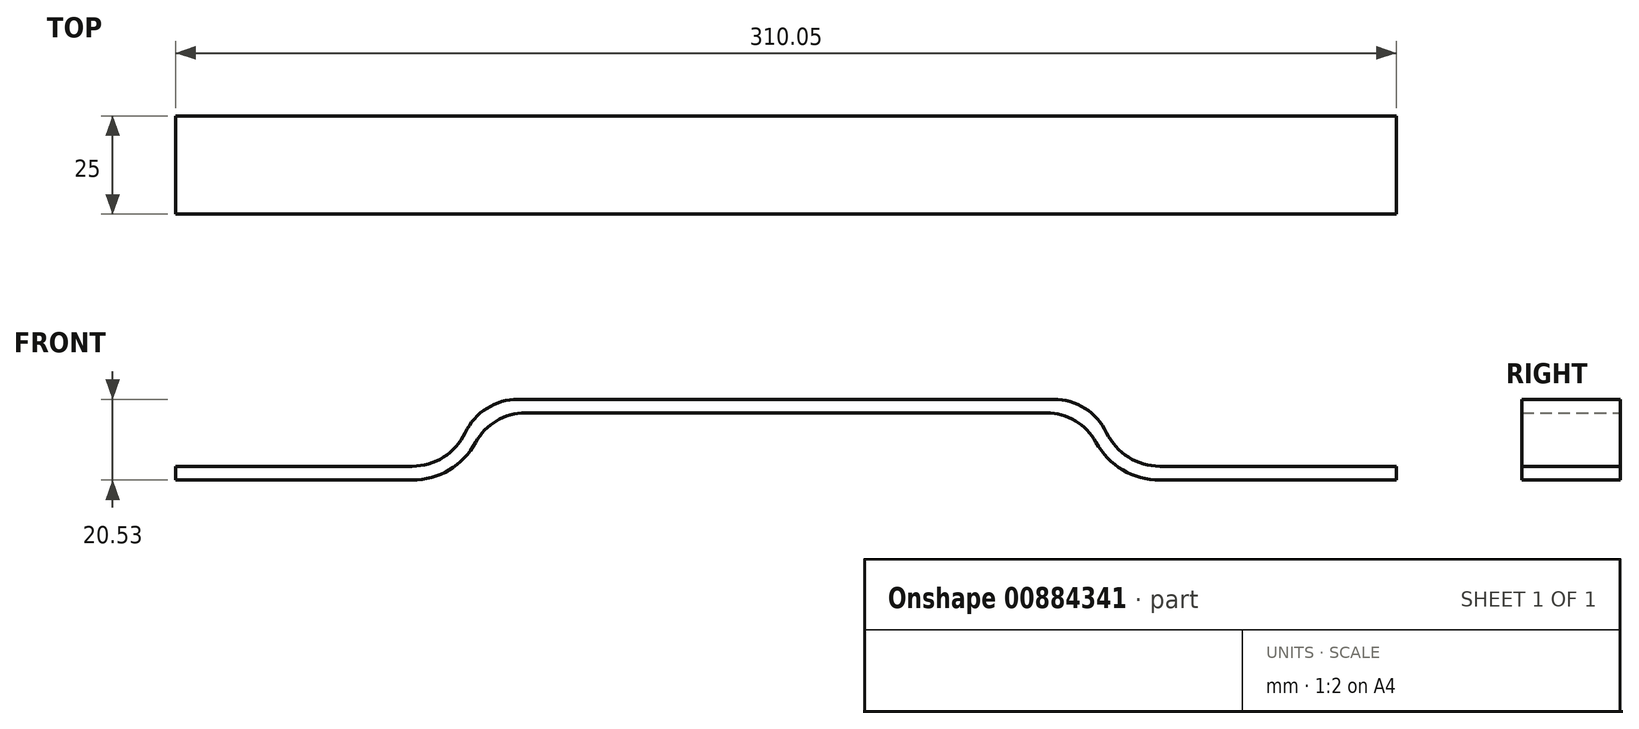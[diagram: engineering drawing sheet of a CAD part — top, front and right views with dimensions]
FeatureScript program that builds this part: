
annotation { "Feature Type Name" : "Feature", "Feature Type Description" : "" }
export const myFeature = defineFeature(function(context is Context, id is Id, definition is map)
    precondition{}
    {
        {
            var Q0;
            Q0=qCreatedBy(makeId("Front.planeOp"),FACE);
            var sketch = newSketch(context, id + "F0", { "sketchPlane" : qUnion([Q0])});
            skLineSegment(sketch, "E0", {"start": v(0, 0) * mm, "end": v(60.07, 0) * mm});
            skArc(sketch, "E1", {"start": v(60.07, 0) * mm, "mid": v(68.04, 2.3) * mm, "end": v(73.55, 8.51) * mm});
            skArc(sketch, "E2", {"start": v(87.03, 17.03) * mm, "mid": v(79.06, 14.72) * mm, "end": v(73.55, 8.51) * mm});
            skLineSegment(sketch, "E3", {"start": v(87.03, 17.03) * mm, "end": v(155.03, 17.03) * mm});
            skLineSegment(sketch, "E4", {"start": v(155.03, 17.03) * mm, "end": v(155.03, -11.24) * mm, "construction": true});
            skLineSegment(sketch, "E5", {"start": v(0, 0) * mm, "end": v(0, -3.5) * mm});
            skLineSegment(sketch, "E6", {"start": v(0, -3.5) * mm, "end": v(60.07, -3.5) * mm});
            skArc(sketch, "E7", {"start": v(60.07, -3.5) * mm, "mid": v(69.46, -0.93) * mm, "end": v(76.23, 6.08) * mm});
            skArc(sketch, "E8", {"start": v(88.8, 13.53) * mm, "mid": v(81.5, 11.52) * mm, "end": v(76.23, 6.08) * mm});
            skLineSegment(sketch, "E9", {"start": v(88.8, 13.53) * mm, "end": v(155.03, 13.53) * mm});
            skLineSegment(sketch, "E10", {"start": v(155.03, 13.53) * mm, "end": v(155.03, 17.03) * mm});
            skLineSegment(sketch, "E11.MirrorCS", {"start": v(223.03, 17.03) * mm, "end": v(155.03, 17.03) * mm});
            skLineSegment(sketch, "E12.MirrorCS", {"start": v(221.25, 13.53) * mm, "end": v(155.03, 13.53) * mm});
            skArc(sketch, "E13.MirrorCS", {"start": v(221.25, 13.53) * mm, "mid": v(228.55, 11.52) * mm, "end": v(233.82, 6.08) * mm});
            skArc(sketch, "E14.MirrorCS", {"start": v(223.03, 17.03) * mm, "mid": v(231, 14.72) * mm, "end": v(236.5, 8.51) * mm});
            skArc(sketch, "E15.MirrorCS", {"start": v(249.98, 0) * mm, "mid": v(242.01, 2.3) * mm, "end": v(236.5, 8.51) * mm});
            skArc(sketch, "E16.MirrorCS", {"start": v(249.98, -3.5) * mm, "mid": v(240.59, -0.93) * mm, "end": v(233.82, 6.08) * mm});
            skLineSegment(sketch, "E17.MirrorCS", {"start": v(310.05, -3.5) * mm, "end": v(249.98, -3.5) * mm});
            skLineSegment(sketch, "E18.MirrorCS", {"start": v(310.05, 0) * mm, "end": v(249.98, 0) * mm});
            skLineSegment(sketch, "E19.MirrorCS", {"start": v(310.05, 0) * mm, "end": v(310.05, -3.5) * mm});
            skSolve(sketch);
        }
        {
            var Q0;
            Q0=makeQuery(id+"F0.imprint","IMPRINT",FACE,{"disambiguationData":[TD([[makeQuery(id+"F0.imprint","IMPRINT",EDGE,{"derivedFrom":sQuery(id+"F0.wireOp",EDGE,"E10")}),-1.0]])]});
            var Q1;
            Q1=makeQuery(id+"F0.imprint","IMPRINT",FACE,{"disambiguationData":[TD([[makeQuery(id+"F0.imprint","IMPRINT",EDGE,{"derivedFrom":sQuery(id+"F0.wireOp",EDGE,"E0")}),-1.0]])]});
            extrude(context, id + "F1", {"entities" : qUnion([Q0, Q1]), "depth" : 25 * mm, "offsetDistance" : 25 * mm});
        }
    });
